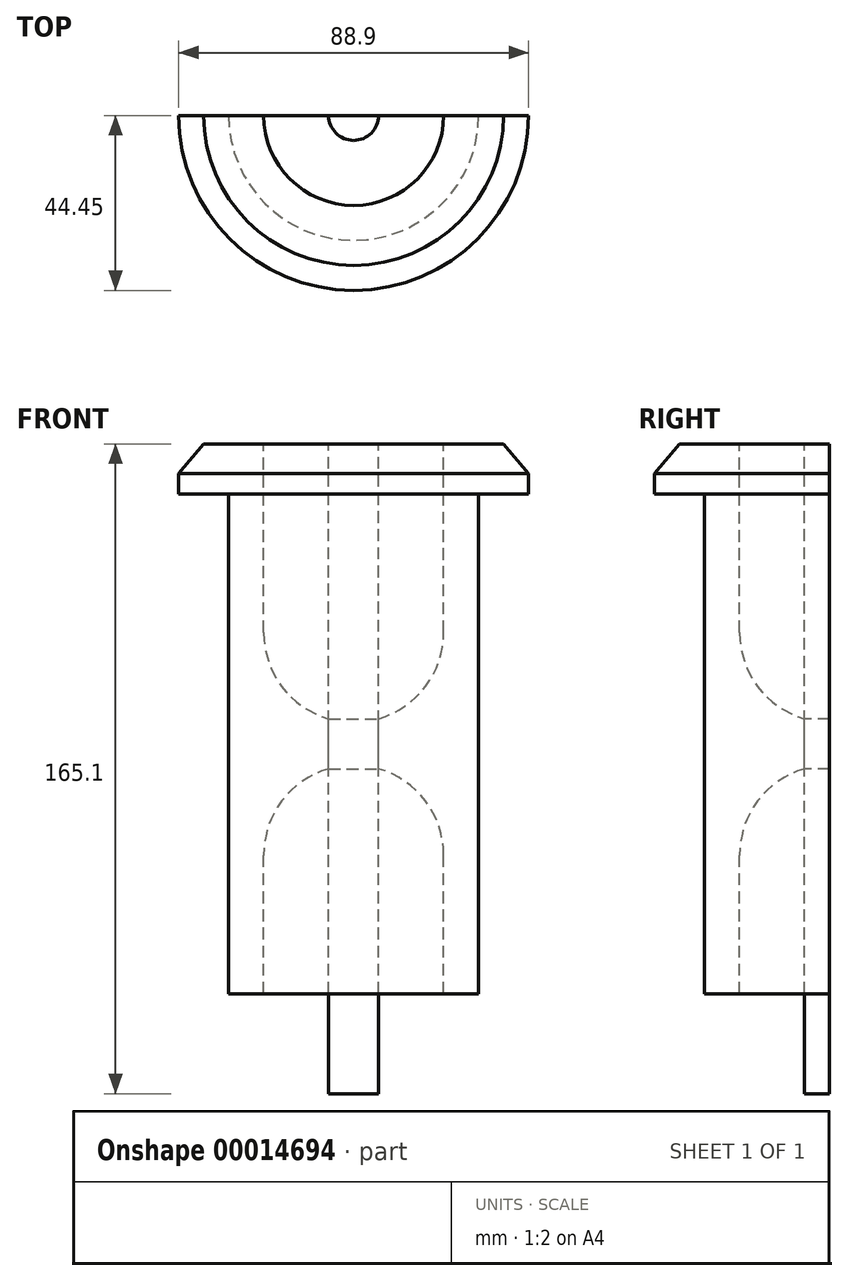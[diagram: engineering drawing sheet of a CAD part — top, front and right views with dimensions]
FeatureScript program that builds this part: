
annotation { "Feature Type Name" : "Feature", "Feature Type Description" : "" }
export const myFeature = defineFeature(function(context is Context, id is Id, definition is map)
    precondition{}
    {
        {
            var Q0;
            Q0=qCreatedBy(makeId("Front.planeOp"),FACE);
            var sketch = newSketch(context, id + "F0", { "sketchPlane" : qUnion([Q0])});
            skLineSegment(sketch, "E0", {"start": v(31.75, 119.47) * mm, "end": v(31.75, -168.69) * mm, "construction": true});
            skLineSegment(sketch, "E1", {"start": v(0, 139.05) * mm, "end": v(0, -174.75) * mm, "construction": true});
            skLineSegment(sketch, "E2", {"start": v(12.7, 126.35) * mm, "end": v(12.7, -144.59) * mm, "construction": true});
            skLineSegment(sketch, "E3", {"start": v(22.86, 147.65) * mm, "end": v(22.86, -139.16) * mm, "construction": true});
            skLineSegment(sketch, "E4", {"start": v(31.75, 63.5) * mm, "end": v(31.75, -63.5) * mm});
            skPoint(sketch, "E5", {"position": v(31.75, 0) * mm});
            skLineSegment(sketch, "E6", {"start": v(31.75, 63.5) * mm, "end": v(22.86, 63.5) * mm});
            skLineSegment(sketch, "E7", {"start": v(22.86, 63.5) * mm, "end": v(22.86, 28.31) * mm});
            skLineSegment(sketch, "E8", {"start": v(0, 0) * mm, "end": v(253.77, 0) * mm, "construction": true});
            skArc(sketch, "E9", {"start": v(22.86, 28.31) * mm, "mid": v(16.16, 12.15) * mm, "end": v(0, 5.45) * mm});
            skLineSegment(sketch, "E10", {"start": v(6.35, 6.35) * mm, "end": v(6.35, 0) * mm});
            skLineSegment(sketch, "E11.MirrorCS", {"start": v(22.86, -63.5) * mm, "end": v(22.86, -28.31) * mm});
            skArc(sketch, "E12.MirrorCS", {"start": v(22.86, -28.31) * mm, "mid": v(16.16, -12.15) * mm, "end": v(0, -5.45) * mm});
            skLineSegment(sketch, "E13.MirrorCS", {"start": v(6.35, -6.35) * mm, "end": v(6.35, 0) * mm});
            skLineSegment(sketch, "E14.MirrorCS", {"start": v(31.75, -63.5) * mm, "end": v(22.86, -63.5) * mm});
            skPoint(sketch, "E15", {"position": v(22.86, 45.9) * mm});
            skPoint(sketch, "E16", {"position": v(22.86, -45.9) * mm});
            skPoint(sketch, "E17", {"position": v(22.86, 88.9) * mm});
            skLineSegment(sketch, "E18", {"start": v(0, 5.45) * mm, "end": v(0, -5.45) * mm});
            skLineSegment(sketch, "E19", {"start": v(48.76, 63.5) * mm, "end": v(38.1, 76.2) * mm});
            skLineSegment(sketch, "E20", {"start": v(48.76, 63.5) * mm, "end": v(6.35, 63.5) * mm});
            skLineSegment(sketch, "E21", {"start": v(6.35, 63.5) * mm, "end": v(6.35, 6.35) * mm});
            skLineSegment(sketch, "E22", {"start": v(38.1, 76.2) * mm, "end": v(0, 76.2) * mm});
            skLineSegment(sketch, "E23", {"start": v(0, 76.2) * mm, "end": v(0, 5.45) * mm});
            skLineSegment(sketch, "E24", {"start": v(6.35, 63.5) * mm, "end": v(0, 63.5) * mm});
            skLineSegment(sketch, "E25", {"start": v(6.35, -6.35) * mm, "end": v(6.35, -63.5) * mm});
            skLineSegment(sketch, "E26", {"start": v(6.35, -63.5) * mm, "end": v(0, -63.5) * mm});
            skLineSegment(sketch, "E27", {"start": v(0, -63.5) * mm, "end": v(0, -5.45) * mm});
            skLineSegment(sketch, "E28.bottom", {"start": v(31.75, -63.5) * mm, "end": v(0, -63.5) * mm});
            skLineSegment(sketch, "E28.top", {"start": v(31.75, -88.9) * mm, "end": v(0, -88.9) * mm});
            skLineSegment(sketch, "E28.left", {"start": v(31.75, -63.5) * mm, "end": v(31.75, -88.9) * mm});
            skLineSegment(sketch, "E28.right", {"start": v(0, -63.5) * mm, "end": v(0, -88.9) * mm});
            skLineSegment(sketch, "E29", {"start": v(6.35, 63.5) * mm, "end": v(6.35, 76.2) * mm});
            skLineSegment(sketch, "E30", {"start": v(6.35, -63.5) * mm, "end": v(6.35, -88.9) * mm});
            skLineSegment(sketch, "E31", {"start": v(22.86, 63.5) * mm, "end": v(22.86, 76.2) * mm});
            skLineSegment(sketch, "E32", {"start": v(22.86, -63.5) * mm, "end": v(22.86, -88.9) * mm});
            skSolve(sketch);
        }
        {
            var Q0;
            {var subQ5=sQuery(id+"F0.wireOp",EDGE,"E4");Q0=makeQuery(id+"F0.imprint","IMPRINT",FACE,{"disambiguationData":[TD([[makeQuery(id+"F0.imprint","IMPRINT",EDGE,{"derivedFrom":subQ5}),-1.0]])]});}
            var Q1;
            {var subQ2=sQuery(id+"F0.wireOp",EDGE,"E19");Q1=makeQuery(id+"F0.imprint","IMPRINT",FACE,{"disambiguationData":[TD([[makeQuery(id+"F0.imprint","IMPRINT",EDGE,{"derivedFrom":subQ2}),1.0]])]});}
            var Q2;
            Q2=sQuery(id+"F0.wireOp",EDGE,"E23");
            revolve(context, id + "F1", {"entities" : qUnion([Q0, Q1]), "axis" : qUnion([Q2]), "revolveType" : RevolveType.FULL});
        }
        {
            var Q0;
            {var subQ1=sQuery(id+"F0.wireOp",EDGE,"E24");Q0=makeQuery(id+"F0.imprint","IMPRINT",FACE,{"disambiguationData":[TD([[makeQuery(id+"F0.imprint","IMPRINT",EDGE,{"derivedFrom":subQ1}),-1.0]])]});}
            var Q1;
            {var subQ1=sQuery(id+"F0.wireOp",EDGE,"E21");Q1=makeQuery(id+"F0.imprint","IMPRINT",FACE,{"disambiguationData":[TD([[makeQuery(id+"F0.imprint","IMPRINT",EDGE,{"derivedFrom":subQ1}),-1.0]])]});}
            var Q2;
            {var subQ2=sQuery(id+"F0.wireOp",EDGE,"E10");Q2=makeQuery(id+"F0.imprint","IMPRINT",FACE,{"disambiguationData":[TD([[makeQuery(id+"F0.imprint","IMPRINT",EDGE,{"derivedFrom":subQ2}),-1.0]])]});}
            var Q3;
            {var subQ2=sQuery(id+"F0.wireOp",EDGE,"E25");Q3=makeQuery(id+"F0.imprint","IMPRINT",FACE,{"disambiguationData":[TD([[makeQuery(id+"F0.imprint","IMPRINT",EDGE,{"derivedFrom":subQ2}),-1.0]])]});}
            var Q4;
            {var subQ1=sQuery(id+"F0.wireOp",EDGE,"E28.right");Q4=makeQuery(id+"F0.imprint","IMPRINT",FACE,{"disambiguationData":[TD([[makeQuery(id+"F0.imprint","IMPRINT",EDGE,{"derivedFrom":subQ1}),1.0]])]});}
            var Q5;
            Q5=sQuery(id+"F0.wireOp",EDGE,"E23");
            revolve(context, id + "F2", {"entities" : qUnion([Q0, Q1, Q2, Q3, Q4]), "axis" : qUnion([Q5]), "revolveType" : RevolveType.FULL});
        }
        {
            var Q0;
            Q0=qCreatedBy(makeId("Top.planeOp"),FACE);
            var sketch = newSketch(context, id + "F3", { "sketchPlane" : qUnion([Q0])});
            skCircle(sketch, "E33", {"center": v(0, 0) * mm, "radius": 44.45 * mm});
            skCircle(sketch, "E34", {"center": v(0, 0) * mm, "radius": 63.5 * mm});
            skSolve(sketch);
        }
        {
            var Q0;
            Q0=makeQuery(id+"F3.imprint","IMPRINT",FACE,{"disambiguationData":[TD([[makeQuery(id+"F3.imprint","IMPRINT",EDGE,{"derivedFrom":sQuery(id+"F3.wireOp",EDGE,"E33")}),-1.0]])]});
            extrude(context, id + "F4", {"entities" : qUnion([Q0]), "operationType" : NewBodyOperationType.REMOVE, "endBound" : BoundingType.THROUGH_ALL, "depth" : 292 * mm});
        }
        {
            var Q0;
            Q0=qCreatedBy(makeId("Front.planeOp"),FACE);
            var sketch = newSketch(context, id + "F5", { "sketchPlane" : qUnion([Q0])});
            skLineSegment(sketch, "E35.bottom", {"start": v(-118.73, 184.85) * mm, "end": v(169.4, 184.85) * mm});
            skLineSegment(sketch, "E35.top", {"start": v(-118.73, -205.01) * mm, "end": v(169.4, -205.01) * mm});
            skLineSegment(sketch, "E35.left", {"start": v(-118.73, 184.85) * mm, "end": v(-118.73, -205.01) * mm});
            skLineSegment(sketch, "E35.right", {"start": v(169.4, 184.85) * mm, "end": v(169.4, -205.01) * mm});
            skSolve(sketch);
        }
        {
            var Q0;
            Q0=makeQuery(id+"F5.imprint","IMPRINT",FACE,{"disambiguationData":[TD([[makeQuery(id+"F5.imprint","IMPRINT",EDGE,{"derivedFrom":sQuery(id+"F5.wireOp",EDGE,"E35.bottom")}),-1.0]])]});
            extrude(context, id + "F6", {"entities" : qUnion([Q0]), "operationType" : NewBodyOperationType.REMOVE, "endBound" : BoundingType.THROUGH_ALL, "oppositeDirection" : true, "depth" : 25.4 * mm});
        }
    });
